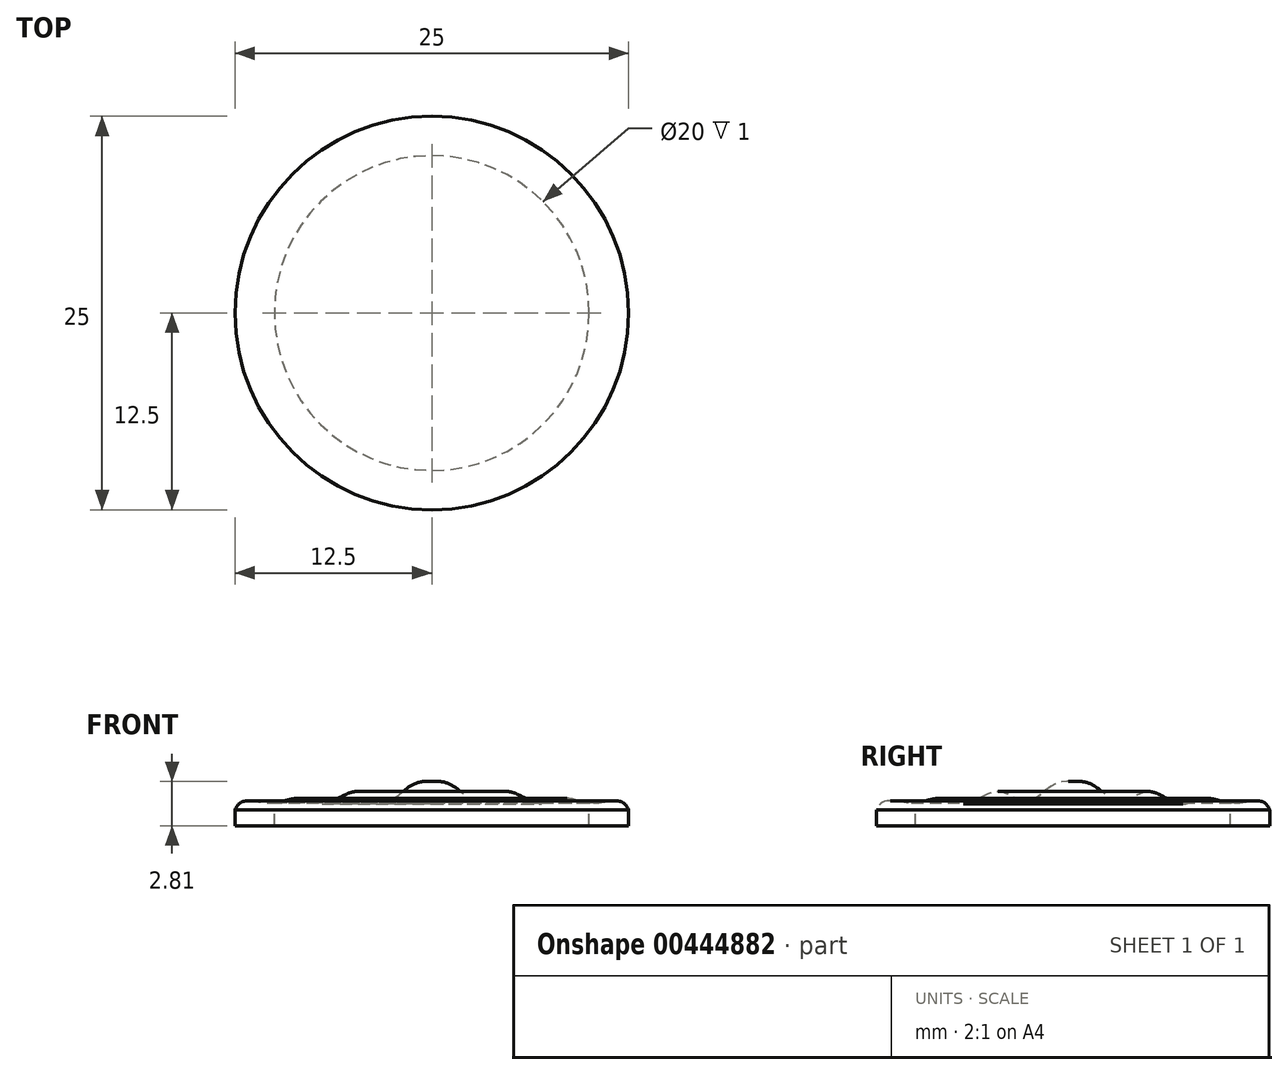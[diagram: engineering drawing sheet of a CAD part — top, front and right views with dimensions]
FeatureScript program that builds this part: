
annotation { "Feature Type Name" : "Feature", "Feature Type Description" : "" }
export const myFeature = defineFeature(function(context is Context, id is Id, definition is map)
    precondition{}
    {
        {
            var Q0;
            Q0=qCreatedBy(makeId("Top.planeOp"),FACE);
            var sketch = newSketch(context, id + "F0", { "sketchPlane" : qUnion([Q0])});
            skCircle(sketch, "E0", {"center": v(0, 0) * mm, "radius": 12.5 * mm});
            skSolve(sketch);
        }
        {
            var Q0;
            Q0 = qSketchRegion(id + "F0", true);
            extrude(context, id + "F1", {"entities" : qUnion([Q0]), "depth" : 0.5 * mm, "hasSecondDirection" : true, "secondDirectionOppositeDirection" : true, "secondDirectionDepth" : 0.5 * mm});
        }
        {
            var Q0;
            Q0=makeQuery(id+"F1.opExtrude","CAP_FACE",FACE,{"disambiguationData":[OSD([sQuery(id+"F0.wireOp",EDGE,"E0")])],"isStart":false});
            var sketch = newSketch(context, id + "F2", { "sketchPlane" : qUnion([Q0])});
            skCircle(sketch, "E1", {"center": v(0, 0) * mm, "radius": 10 * mm});
            skSolve(sketch);
        }
        {
            var Q0;
            Q0 = qSketchRegion(id + "F2", true);
            extrude(context, id + "F3", {"entities" : qUnion([Q0]), "operationType" : NewBodyOperationType.REMOVE, "oppositeDirection" : true, "depth" : 25 * mm});
        }
        {
            var Q0;
            Q0=qCreatedBy(makeId("Right.planeOp"),FACE);
            var sketch = newSketch(context, id + "F4", { "sketchPlane" : qUnion([Q0])});
            skLineSegment(sketch, "E2.0", {"start": v(-12.5, 0.5) * mm, "end": v(12.5, 0.5) * mm});
            skLineSegment(sketch, "E3", {"start": v(0, 0.5) * mm, "end": v(0, 2.3) * mm});
            skFitSpline(sketch, "E4", {"points": [v(0, 2.3) * mm, v(-1.47, 1.94) * mm, v(-3.01, 1) * mm, v(-4.72, 1.67) * mm, v(-6.8, 0.9) * mm, v(-8.49, 1.23) * mm, v(-10.35, 0.93) * mm, v(-12.5, 0.5) * mm], "startDerivative": vector(-13.7, 1.19) * mm, "endDerivative": vector(-7.52, -18.47) * mm});
            skSolve(sketch);
        }
        {
            var Q0;
            {var subQ2=sQuery(id+"F4.wireOp",EDGE,"E3");Q0=makeQuery(id+"F4.imprint","IMPRINT",FACE,{"disambiguationData":[TD([[makeQuery(id+"F4.imprint","IMPRINT",EDGE,{"derivedFrom":subQ2}),1.0]])]});}
            var Q1;
            Q1=sQuery(id+"F4.wireOp",EDGE,"E3");
            revolve(context, id + "F5", {"operationType" : NewBodyOperationType.ADD, "entities" : qUnion([Q0]), "axis" : qUnion([Q1]), "revolveType" : RevolveType.FULL});
        }
    });
